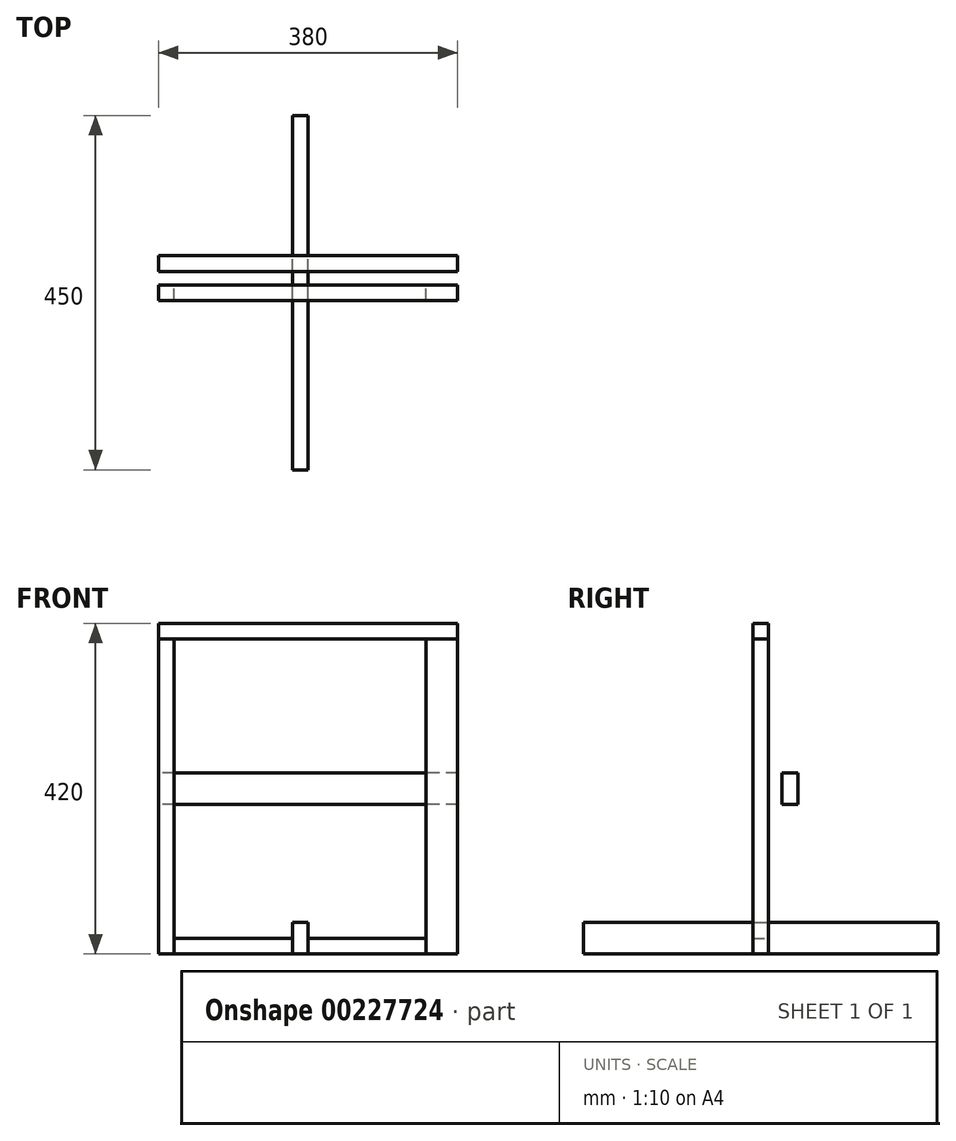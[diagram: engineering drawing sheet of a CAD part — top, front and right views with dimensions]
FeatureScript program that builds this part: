
annotation { "Feature Type Name" : "Feature", "Feature Type Description" : "" }
export const myFeature = defineFeature(function(context is Context, id is Id, definition is map)
    precondition{}
    {
        {
            var Q0;
            Q0=qCreatedBy(makeId("Top.planeOp"),FACE);
            var sketch = newSketch(context, id + "F0", { "sketchPlane" : qUnion([Q0])});
            skLineSegment(sketch, "E0.bottom", {"start": v(10, -225) * mm, "end": v(-10, -225) * mm});
            skLineSegment(sketch, "E0.top", {"start": v(10, 225) * mm, "end": v(-10, 225) * mm});
            skLineSegment(sketch, "E0.left", {"start": v(10, -225) * mm, "end": v(10, 225) * mm});
            skLineSegment(sketch, "E0.right", {"start": v(-10, -225) * mm, "end": v(-10, 225) * mm});
            skPoint(sketch, "E0.middle", {"position": v(0, 0) * mm});
            skLineSegment(sketch, "E1.bottom", {"start": v(160, -10) * mm, "end": v(10, -10) * mm});
            skLineSegment(sketch, "E1.top", {"start": v(160, 10) * mm, "end": v(10, 10) * mm});
            skLineSegment(sketch, "E1.left", {"start": v(160, -10) * mm, "end": v(160, 10) * mm});
            skLineSegment(sketch, "E1.right", {"start": v(-160, -10) * mm, "end": v(-160, 10) * mm});
            skLineSegment(sketch, "E2.trimOffspring", {"start": v(-10, 10) * mm, "end": v(-160, 10) * mm});
            skLineSegment(sketch, "E3.trimOffspring", {"start": v(-10, -10) * mm, "end": v(-160, -10) * mm});
            skLineSegment(sketch, "E4.bottom", {"start": v(-160, 10) * mm, "end": v(-180, 10) * mm});
            skLineSegment(sketch, "E4.top", {"start": v(-160, -10) * mm, "end": v(-180, -10) * mm});
            skLineSegment(sketch, "E4.left", {"start": v(-160, 10) * mm, "end": v(-160, -10) * mm});
            skLineSegment(sketch, "E4.right", {"start": v(-180, 10) * mm, "end": v(-180, -10) * mm});
            skLineSegment(sketch, "E5", {"start": v(0, 0) * mm, "end": v(0, 36.26) * mm, "construction": true});
            skLineSegment(sketch, "E6.bottom", {"start": v(160, 10) * mm, "end": v(200, 10) * mm});
            skLineSegment(sketch, "E6.top", {"start": v(160, -10) * mm, "end": v(200, -10) * mm});
            skLineSegment(sketch, "E6.left", {"start": v(160, 10) * mm, "end": v(160, -10) * mm});
            skLineSegment(sketch, "E6.right", {"start": v(200, 10) * mm, "end": v(200, -10) * mm});
            skSolve(sketch);
        }
        {
            var Q0;
            Q0=makeQuery(id+"F0.imprint","IMPRINT",FACE,{"disambiguationData":[TD([[makeQuery(id+"F0.imprint","IMPRINT",EDGE,{"derivedFrom":sQuery(id+"F0.wireOp",EDGE,"E0.bottom")}),-1.0]])]});
            extrude(context, id + "F1", {"entities" : qUnion([Q0]), "depth" : 40 * mm});
        }
        {
            var Q0;
            {var subQ0=sQuery(id+"F0.wireOp",EDGE,"E2.trimOffspring");Q0=makeQuery(id+"F0.imprint","IMPRINT",FACE,{"disambiguationData":[TD([[makeQuery(id+"F0.imprint","IMPRINT",EDGE,{"derivedFrom":subQ0}),1.0]])]});}
            var Q1;
            {var subQ0=sQuery(id+"F0.wireOp",EDGE,"E1.bottom");Q1=makeQuery(id+"F0.imprint","IMPRINT",FACE,{"disambiguationData":[TD([[makeQuery(id+"F0.imprint","IMPRINT",EDGE,{"derivedFrom":subQ0}),-1.0]])]});}
            extrude(context, id + "F2", {"entities" : qUnion([Q0, Q1]), "depth" : 20 * mm});
        }
        {
            var Q0;
            Q0=makeQuery(id+"F0.imprint","IMPRINT",FACE,{"disambiguationData":[TD([[makeQuery(id+"F0.imprint","IMPRINT",EDGE,{"derivedFrom":sQuery(id+"F0.wireOp",EDGE,"E4.bottom")}),1.0]])]});
            var Q1;
            Q1=makeQuery(id+"F0.imprint","IMPRINT",FACE,{"disambiguationData":[TD([[makeQuery(id+"F0.imprint","IMPRINT",EDGE,{"derivedFrom":sQuery(id+"F0.wireOp",EDGE,"E1.left")}),-1.0]])]});
            var Q2;
            Q2=makeQuery(id+"F0.imprint","IMPRINT",FACE,{"disambiguationData":[TD([[makeQuery(id+"F0.imprint","IMPRINT",EDGE,{"derivedFrom":sQuery(id+"F0.wireOp",EDGE,"E6.bottom")}),-1.0]])]});
            extrude(context, id + "F3", {"entities" : qUnion([Q0, Q1, Q2]), "depth" : 400 * mm});
        }
        {
            var Q0;
            Q0=makeQuery(id+"F3.opExtrude","CAP_FACE",FACE,{"disambiguationData":[OSD([sQuery(id+"F0.wireOp",EDGE,"E4.bottom"),sQuery(id+"F0.wireOp",EDGE,"E4.top"),sQuery(id+"F0.wireOp",EDGE,"E4.left"),sQuery(id+"F0.wireOp",EDGE,"E4.right")])],"isStart":false});
            var sketch = newSketch(context, id + "F4", { "sketchPlane" : qUnion([Q0])});
            skPoint(sketch, "E7.0", {"position": v(-180, 10) * mm});
            skPoint(sketch, "E8.0", {"position": v(200, -10) * mm});
            skLineSegment(sketch, "E9.bottom", {"start": v(-180, 10) * mm, "end": v(200, 10) * mm});
            skLineSegment(sketch, "E9.top", {"start": v(-180, -10) * mm, "end": v(200, -10) * mm});
            skLineSegment(sketch, "E9.left", {"start": v(-180, 10) * mm, "end": v(-180, -10) * mm});
            skLineSegment(sketch, "E9.right", {"start": v(200, 10) * mm, "end": v(200, -10) * mm});
            skSolve(sketch);
        }
        {
            var Q0;
            {var subQ2=sQuery(id+"F4.wireOp",EDGE,"E9.right");Q0=makeQuery(id+"F4.imprint","IMPRINT",FACE,{"disambiguationData":[TD([[makeQuery(id+"F4.imprint","IMPRINT",EDGE,{"derivedFrom":subQ2}),-1.0]])]});}
            var Q1;
            {var subQ2=sQuery(id+"F4.wireOp",EDGE,"E9.left");Q1=makeQuery(id+"F4.imprint","IMPRINT",FACE,{"disambiguationData":[TD([[makeQuery(id+"F4.imprint","IMPRINT",EDGE,{"derivedFrom":subQ2}),1.0]])]});}
            extrude(context, id + "F5", {"entities" : qUnion([Q0, Q1]), "depth" : 20 * mm});
        }
        {
            var Q0;
            Q0=makeQuery(id+"F3.opExtrude","SWEPT_FACE",FACE,{"disambiguationData":[OSD([sQuery(id+"F0.wireOp",EDGE,"E6.bottom")])]});
            cPlane(context, id + "F6", {"entities" : qUnion([Q0]), "cplaneType" : CPlaneType.OFFSET, "offset" : 17 * mm, "width" : 150 * mm, "height" : 150 * mm});
        }
        {
            var Q0;
            Q0=qCreatedBy(id+"F6.planeOp",FACE);
            var sketch = newSketch(context, id + "F7", { "sketchPlane" : qUnion([Q0])});
            skLineSegment(sketch, "E10.bottom", {"start": v(-200, 230) * mm, "end": v(180, 230) * mm});
            skLineSegment(sketch, "E10.top", {"start": v(-200, 190) * mm, "end": v(180, 190) * mm});
            skLineSegment(sketch, "E10.left", {"start": v(-200, 230) * mm, "end": v(-200, 190) * mm});
            skLineSegment(sketch, "E10.right", {"start": v(180, 230) * mm, "end": v(180, 190) * mm});
            skSolve(sketch);
        }
        {
            var Q0;
            Q0 = qSketchRegion(id + "F7", true);
            extrude(context, id + "F8", {"entities" : qUnion([Q0]), "depth" : 20 * mm, "offsetDistance" : 25 * mm});
        }
    });
